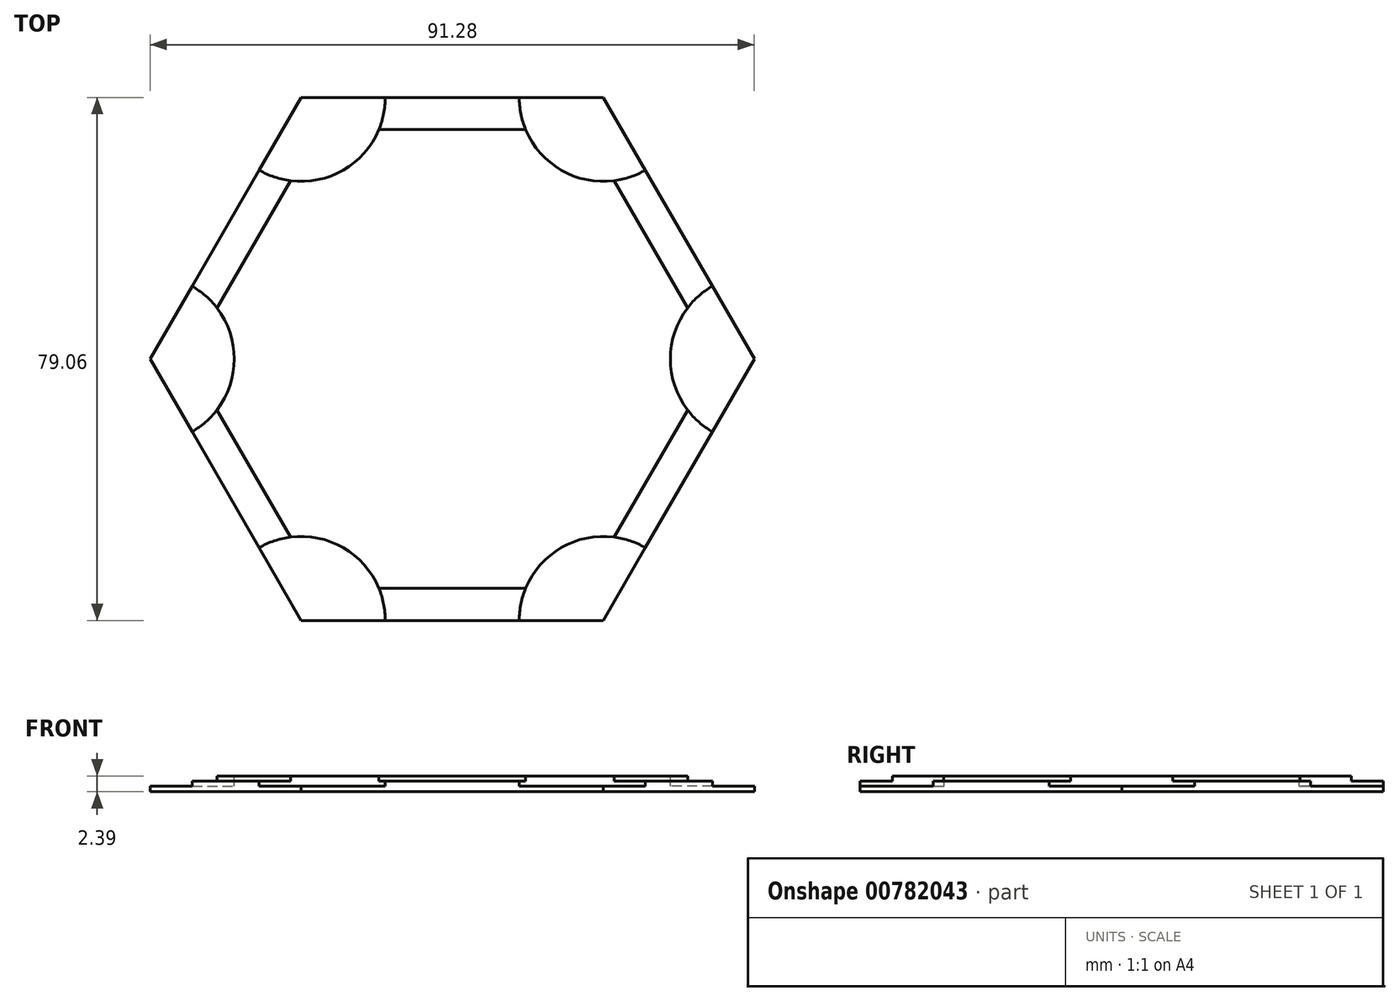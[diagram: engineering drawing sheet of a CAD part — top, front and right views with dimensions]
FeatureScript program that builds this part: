
annotation { "Feature Type Name" : "Feature", "Feature Type Description" : "" }
export const myFeature = defineFeature(function(context is Context, id is Id, definition is map)
    precondition{}
    {
        {
            var Q0;
            Q0=qCreatedBy(makeId("Top.planeOp"),FACE);
            var sketch = newSketch(context, id + "F0", { "sketchPlane" : qUnion([Q0])});
            skLineSegment(sketch, "E0", {"start": v(22.82, -39.53) * mm, "end": v(-22.82, -39.53) * mm});
            skLineSegment(sketch, "E1", {"start": v(-22.82, -39.53) * mm, "end": v(-45.64, 0) * mm});
            skLineSegment(sketch, "E2", {"start": v(-45.64, 0) * mm, "end": v(-22.82, 39.53) * mm});
            skLineSegment(sketch, "E3", {"start": v(-22.82, 39.53) * mm, "end": v(22.82, 39.53) * mm});
            skLineSegment(sketch, "E4", {"start": v(45.64, 0) * mm, "end": v(22.82, -39.53) * mm});
            skLineSegment(sketch, "E5", {"start": v(22.82, 39.53) * mm, "end": v(45.64, 0) * mm});
            skLineSegment(sketch, "E6", {"start": v(-22.82, -39.53) * mm, "end": v(22.82, 39.53) * mm, "construction": true});
            skSolve(sketch);
        }
        {
            var Q0;
            Q0=qSketchRegion(id+"F0",true);
            extrude(context, id + "F1", {"entities" : qUnion([Q0]), "depth" : 1.63 * mm, "offsetDistance" : 25.4 * mm});
        }
        {
            var Q0;
            Q0=qCreatedBy(makeId("Top.planeOp"),FACE);
            var sketch = newSketch(context, id + "F2", { "sketchPlane" : qUnion([Q0])});
            skLineSegment(sketch, "E7.0", {"start": v(20, -34.65) * mm, "end": v(40.01, 0) * mm});
            skLineSegment(sketch, "E7.1", {"start": v(20, 34.65) * mm, "end": v(-20, 34.65) * mm});
            skLineSegment(sketch, "E7.2", {"start": v(-20, 34.65) * mm, "end": v(-40.01, 0) * mm});
            skLineSegment(sketch, "E7.3", {"start": v(40.01, 0) * mm, "end": v(20, 34.65) * mm});
            skLineSegment(sketch, "E7.4", {"start": v(-40.01, 0) * mm, "end": v(-20, -34.65) * mm});
            skLineSegment(sketch, "E7.5", {"start": v(-20, -34.65) * mm, "end": v(20, -34.65) * mm});
            skLineSegment(sketch, "E8.0", {"start": v(19.16, -33.18) * mm, "end": v(38.31, 0) * mm});
            skLineSegment(sketch, "E8.1", {"start": v(19.16, 33.18) * mm, "end": v(-19.16, 33.18) * mm});
            skLineSegment(sketch, "E8.2", {"start": v(-19.16, 33.18) * mm, "end": v(-38.31, 0) * mm});
            skLineSegment(sketch, "E8.4", {"start": v(-38.31, 0) * mm, "end": v(-19.16, -33.18) * mm});
            skLineSegment(sketch, "E8.5", {"start": v(-19.16, -33.18) * mm, "end": v(19.16, -33.18) * mm});
            skSolve(sketch);
        }
        {
            var Q0;
            Q0=qSketchRegion(id+"F2",true);
            extrude(context, id + "F3", {"entities" : qUnion([Q0]), "operationType" : NewBodyOperationType.ADD, "depth" : 2.4 * mm, "offsetDistance" : 25.4 * mm});
        }
        {
            var Q0;
            Q0=makeQuery(id+"F3.opExtrude","CAP_FACE",FACE,{"disambiguationData":[OSD([sQuery(id+"F2.wireOp",EDGE,"E7.0"),sQuery(id+"F2.wireOp",EDGE,"E7.1"),sQuery(id+"F2.wireOp",EDGE,"E7.2"),sQuery(id+"F2.wireOp",EDGE,"E7.3"),sQuery(id+"F2.wireOp",EDGE,"E7.4"),sQuery(id+"F2.wireOp",EDGE,"E7.5")])],"isStart":false});
            var sketch = newSketch(context, id + "F4", { "sketchPlane" : qUnion([Q0])});
            skSolve(sketch);
        }
        {
            var Q0;
            Q0=makeQuery(id+"F4.imprint","IMPRINT",FACE,{"disambiguationData":[TD([[makeQuery(id+"F4.imprint","IMPRINT",EDGE,{"derivedFrom":makeQuery(id+"F3.opExtrude","CAP_EDGE",EDGE,{"disambiguationData":[OSD([sQuery(id+"F2.wireOp",EDGE,"E7.0")])],"isStart":false})}),1.0]])]});
            var sketch = newSketch(context, id + "F5", { "sketchPlane" : qUnion([Q0])});
            skCircle(sketch, "E9", {"center": v(22.82, -39.53) * mm, "radius": 12.7 * mm});
            skCircle(sketch, "E10", {"center": v(45.64, 0) * mm, "radius": 12.7 * mm});
            skCircle(sketch, "E11", {"center": v(22.82, 39.53) * mm, "radius": 12.7 * mm});
            skCircle(sketch, "E12", {"center": v(-22.82, 39.53) * mm, "radius": 12.7 * mm});
            skCircle(sketch, "E13", {"center": v(-45.64, 0) * mm, "radius": 12.7 * mm});
            skCircle(sketch, "E14", {"center": v(-22.82, -39.53) * mm, "radius": 12.7 * mm});
            skSolve(sketch);
        }
        {
            var Q0;
            Q0=qSketchRegion(id+"F5",true);
            extrude(context, id + "F6", {"entities" : qUnion([Q0]), "operationType" : NewBodyOperationType.REMOVE, "oppositeDirection" : true, "depth" : 1.52 * mm, "offsetDistance" : 25.4 * mm});
        }
    });
